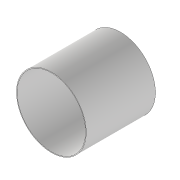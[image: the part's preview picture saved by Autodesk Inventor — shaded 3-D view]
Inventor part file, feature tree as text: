
AUTODESK INVENTOR PART (.ipt)
format: ipt  version: 2020 (Build 240168000, 168)  size: 117,760 bytes
history: native  units: mm
features: sketch x2, revolve x1, extrude x1
ambient origin geometry x8: Origin, YZ Plane, XZ Plane, XY Plane, X Axis, Y Axis, Z Axis, Center Point
bodies: Volumenkörper1 (feature_tree)
feature tree (4):
  revolve  "Umdrehung1"
  extrude  "Extrusion1"  Depth=5.0mm
  sketch  "Skizze1"  dims[d0=5.0mm d1=5.0mm]
  sketch  "Skizze2"  dims[d2=5.0mm d3=500.0mm d4=500.0mm d5=250.0mm d6=100.0mm d7=90.0deg d8=100.0mm d9=190.0mm d10=0.0mm d11=0.0mm]
